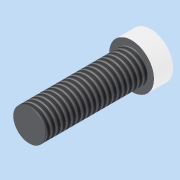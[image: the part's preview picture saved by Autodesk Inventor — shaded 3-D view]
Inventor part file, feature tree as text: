
AUTODESK INVENTOR PART (.ipt)
format: ipt  version: 2015 (Build 190159000, 159)  size: 105,472 bytes
history: native  units: mm
features: sketch x2, revolve x1, thread x1, extrude x1
ambient origin geometry x8: Origin, YZ Plane, XZ Plane, XY Plane, X Axis, Y Axis, Z Axis, Center Point
bodies: Solid1 (feature_tree)
feature tree (5):
  revolve  "Revolution1"  [1 undecoded]
  thread  "Thread1"  [1 undecoded]
  extrude  "Extrusion1"  TaperAngle=90.0deg  [1 undecoded]
  sketch  "Sketch1"  dims[d0=2.5mm d1=3.0mm d2=3.5mm]
  sketch  "Sketch2"  dims[d3=16.0mm d4=90.0deg d5=10.0mm d6=0.0mm d7=2.0mm d8=0.0mm]
note: 3 required parameter values undecoded (feature->parameter linkage not recoverable at this tier; creation-order binding heuristic only, values carry confidence <= 0.55)